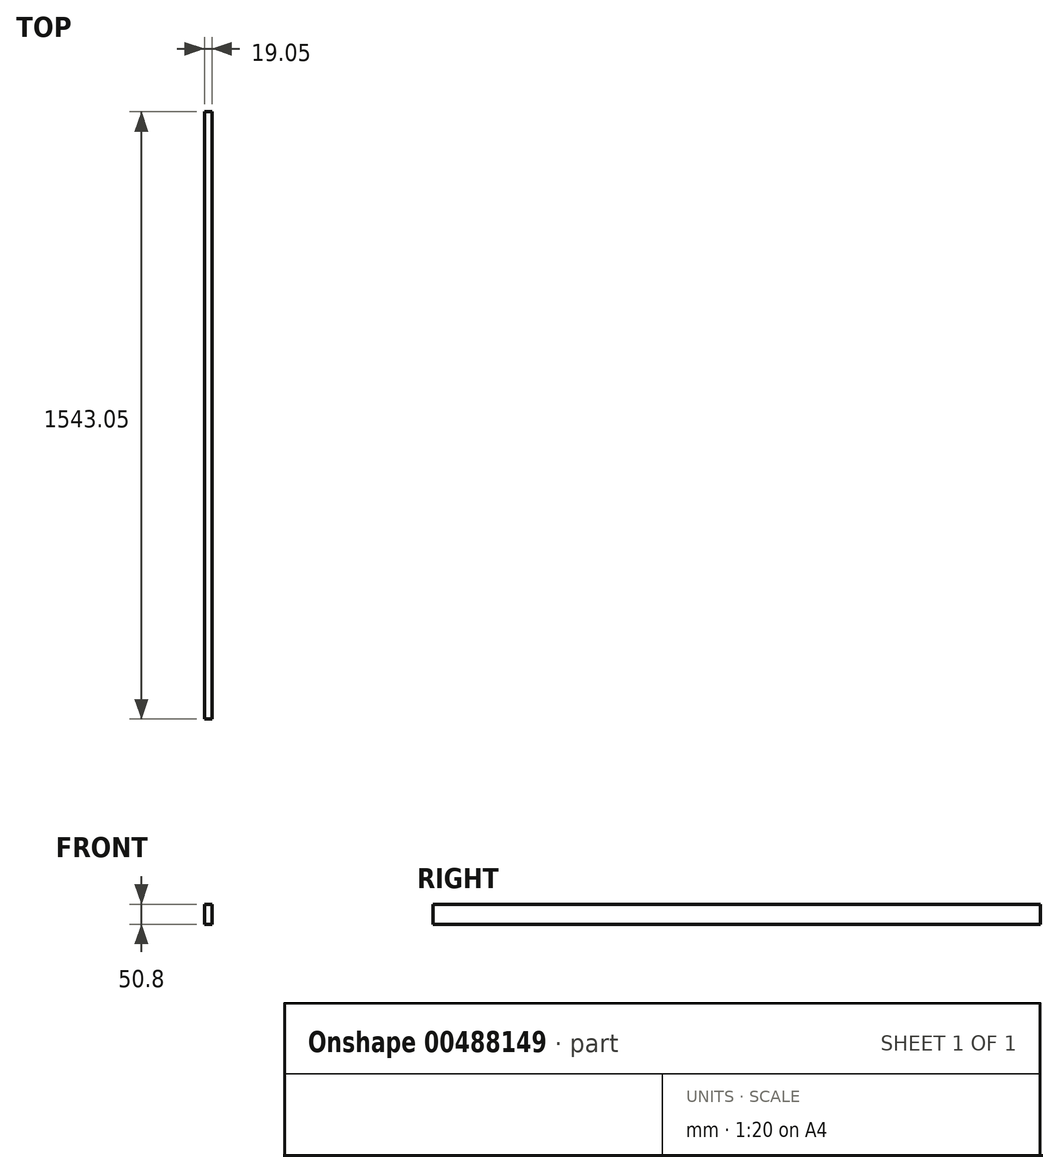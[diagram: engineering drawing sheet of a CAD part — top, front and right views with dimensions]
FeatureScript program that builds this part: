
annotation { "Feature Type Name" : "Feature", "Feature Type Description" : "" }
export const myFeature = defineFeature(function(context is Context, id is Id, definition is map)
    precondition{}
    {
        {
            var Q0;
            Q0=qCreatedBy(makeId("Front.planeOp"),FACE);
            var sketch = newSketch(context, id + "F0", { "sketchPlane" : qUnion([Q0])});
            skLineSegment(sketch, "E0", {"start": v(0, 0) * mm, "end": v(19.05, 0) * mm});
            skLineSegment(sketch, "E1", {"start": v(0, 0) * mm, "end": v(0, -50.8) * mm});
            skLineSegment(sketch, "E2", {"start": v(0, -50.8) * mm, "end": v(19.05, -50.8) * mm});
            skLineSegment(sketch, "E3", {"start": v(19.05, -50.8) * mm, "end": v(19.05, 0) * mm});
            skSolve(sketch);
        }
        {
            var Q0;
            Q0=makeQuery(id+"F0.imprint","IMPRINT",FACE,{"disambiguationData":[TD([[makeQuery(id+"F0.imprint","IMPRINT",EDGE,{"derivedFrom":sQuery(id+"F0.wireOp",EDGE,"E0")}),-1.0]])]});
            extrude(context, id + "F1", {"entities" : qUnion([Q0]), "oppositeDirection" : true, "depth" : 1543.05 * mm, "offsetDistance" : 25.4 * mm});
        }
    });
